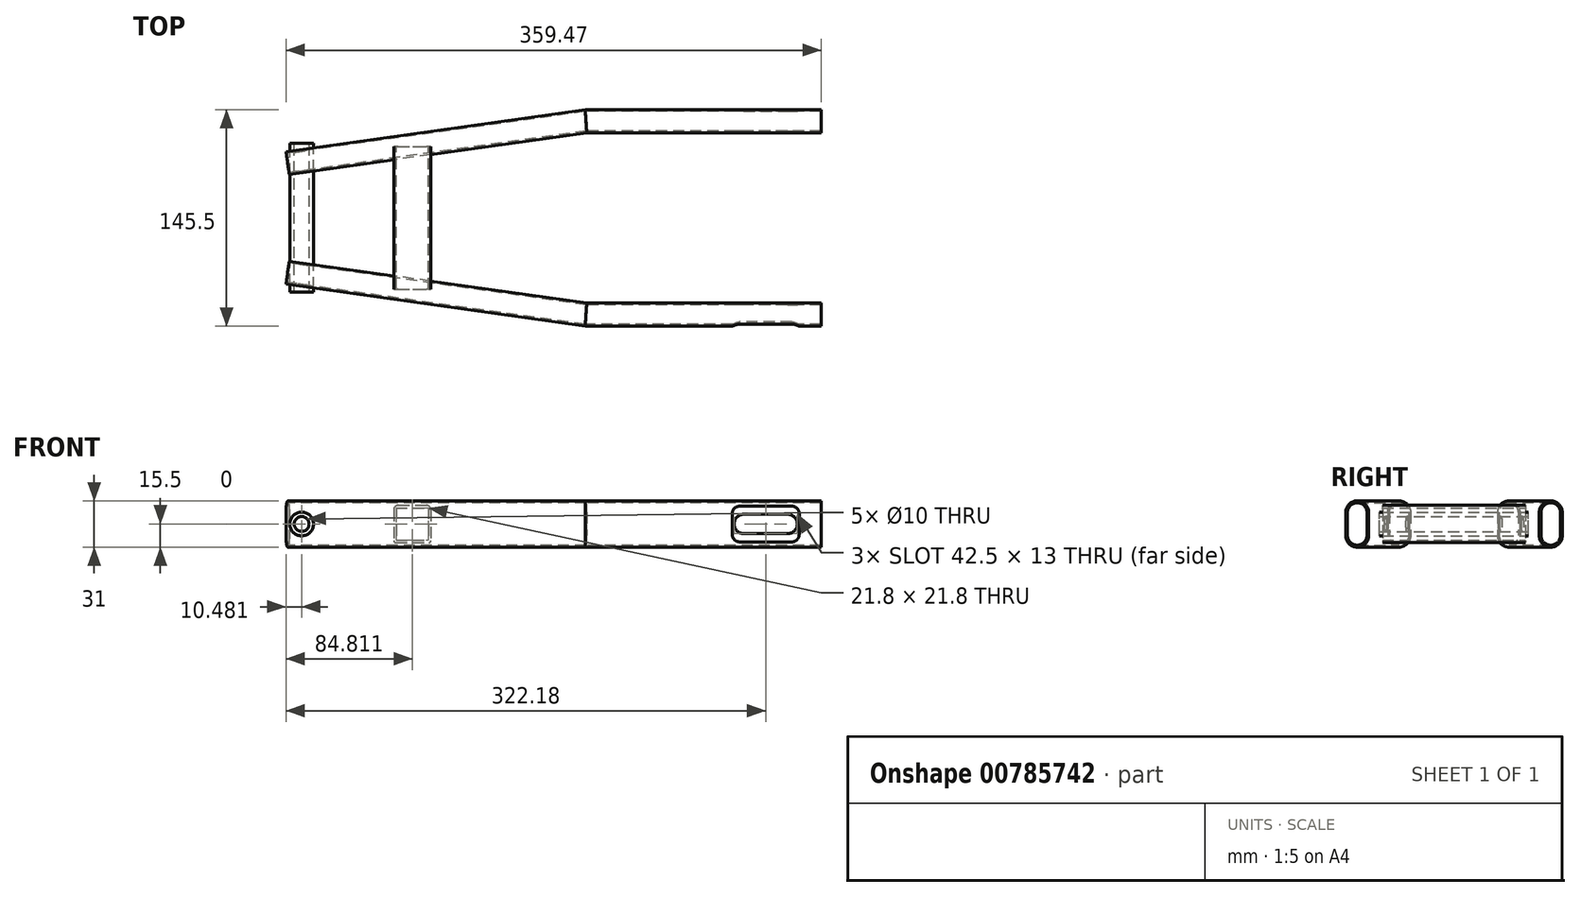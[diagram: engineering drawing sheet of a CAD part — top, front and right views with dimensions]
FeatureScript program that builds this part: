
annotation { "Feature Type Name" : "Feature", "Feature Type Description" : "" }
export const myFeature = defineFeature(function(context is Context, id is Id, definition is map)
    precondition{}
    {
        {
            var Q0;
            Q0=qCreatedBy(makeId("Top.planeOp"),FACE);
            var sketch = newSketch(context, id + "F0", { "sketchPlane" : qUnion([Q0])});
            skLineSegment(sketch, "E0", {"start": v(0, 65) * mm, "end": v(-158, 65) * mm});
            skLineSegment(sketch, "E1", {"start": v(-158, 65) * mm, "end": v(-358.4, 36.84) * mm});
            skSolve(sketch);
        }
        {
            var Q0;
            Q0=qCreatedBy(makeId("Right.planeOp"),FACE);
            var sketch = newSketch(context, id + "F1", { "sketchPlane" : qUnion([Q0])});
            skLineSegment(sketch, "E2.left", {"start": v(57.25, 7.75) * mm, "end": v(57.25, -7.75) * mm});
            skLineSegment(sketch, "E2.right", {"start": v(72.75, 7.75) * mm, "end": v(72.75, -7.75) * mm});
            skPoint(sketch, "E2.middle", {"position": v(65, 0) * mm});
            skArc(sketch, "E3", {"start": v(57.25, -7.75) * mm, "mid": v(65, -15.5) * mm, "end": v(72.75, -7.75) * mm});
            skArc(sketch, "E4", {"start": v(57.25, 7.75) * mm, "mid": v(65, 15.5) * mm, "end": v(72.75, 7.75) * mm});
            skLineSegment(sketch, "E5.0", {"start": v(71.55, 7.75) * mm, "end": v(71.55, -7.75) * mm});
            skLineSegment(sketch, "E6.0", {"start": v(58.45, 7.75) * mm, "end": v(58.45, -7.75) * mm});
            skArc(sketch, "E7.0", {"start": v(58.45, 7.75) * mm, "mid": v(65, 14.3) * mm, "end": v(71.55, 7.75) * mm});
            skArc(sketch, "E8.0", {"start": v(58.45, -7.75) * mm, "mid": v(65, -14.3) * mm, "end": v(71.55, -7.75) * mm});
            skSolve(sketch);
        }
        {
            var Q0;
            Q0=qSketchRegion(id+"F1",true);
            var Q1;
            Q1=qConstructionFilter(qBodyType(qCreatedBy(id+"F0",EDGE),BodyType.WIRE),ConstructionObject.NO);
            sweep(context, id + "F2", {"profiles" : qUnion([Q0]), "path" : qUnion([Q1])});
        }
        {
            var Q0;
            Q0=makeQuery(id+"F2.opSweep","SWEPT_BODY",BODY,{"disambiguationData":[OSD([sQuery(id+"F0.wireOp",EDGE,"E1"),sQuery(id+"F1.wireOp",EDGE,"E2.left"),sQuery(id+"F1.wireOp",EDGE,"E2.right"),sQuery(id+"F1.wireOp",EDGE,"E3"),sQuery(id+"F1.wireOp",EDGE,"E4"),sQuery(id+"F1.wireOp",EDGE,"E5.0"),sQuery(id+"F1.wireOp",EDGE,"E6.0"),sQuery(id+"F1.wireOp",EDGE,"E7.0"),sQuery(id+"F1.wireOp",EDGE,"E8.0")])]});
            var Q1;
            Q1=qCreatedBy(makeId("Front.planeOp"),FACE);
            mirror(context, id + "F3", {"entities" : qUnion([Q0]), "mirrorPlane" : qUnion([Q1])});
        }
        {
            var Q0;
            Q0=qCreatedBy(makeId("Front.planeOp"),FACE);
            var sketch = newSketch(context, id + "F4", { "sketchPlane" : qUnion([Q0])});
            skLineSegment(sketch, "E9.bottom", {"start": v(-52.04, 6.5) * mm, "end": v(-22.54, 6.5) * mm});
            skLineSegment(sketch, "E9.top", {"start": v(-52.04, -6.5) * mm, "end": v(-22.54, -6.5) * mm});
            skLineSegment(sketch, "E9.left", {"start": v(-52.04, 6.5) * mm, "end": v(-52.04, -6.5) * mm});
            skLineSegment(sketch, "E9.right", {"start": v(-22.54, 6.5) * mm, "end": v(-22.54, -6.5) * mm});
            skPoint(sketch, "E9.middle", {"position": v(-37.3, 0) * mm});
            skArc(sketch, "E10", {"start": v(-22.54, 6.5) * mm, "mid": v(-16.04, 0) * mm, "end": v(-22.54, -6.5) * mm});
            skArc(sketch, "E11", {"start": v(-52.04, 6.5) * mm, "mid": v(-58.54, 0) * mm, "end": v(-52.04, -6.5) * mm});
            skSolve(sketch);
        }
        {
            var Q0;
            Q0=qSketchRegion(id+"F4",true);
            extrude(context, id + "F5", {"entities" : qUnion([Q0]), "operationType" : NewBodyOperationType.REMOVE, "depth" : 99 * mm, "offsetDistance" : 25 * mm});
        }
        {
            var Q0;
            Q0=qSketchRegion(id+"F4",true);
            extrude(context, id + "F6", {"entities" : qUnion([Q0]), "operationType" : NewBodyOperationType.REMOVE, "oppositeDirection" : true, "depth" : 86 * mm, "offsetDistance" : 25 * mm});
        }
        {
            var Q0;
            Q0=qCreatedBy(makeId("Front.planeOp"),FACE);
            var sketch = newSketch(context, id + "F7", { "sketchPlane" : qUnion([Q0])});
            skCircle(sketch, "E12", {"center": v(-348.99, 0) * mm, "radius": 8 * mm});
            skCircle(sketch, "E13", {"center": v(-348.99, 0) * mm, "radius": 5 * mm});
            skSolve(sketch);
        }
        {
            var Q0;
            Q0=qSketchRegion(id+"F7",true);
            extrude(context, id + "F8", {"entities" : qUnion([Q0]), "endBound" : BoundingType.SYMMETRIC, "depth" : 100 * mm, "offsetDistance" : 25 * mm});
        }
        {
            var Q0;
            Q0=qCreatedBy(makeId("Front.planeOp"),FACE);
            var sketch = newSketch(context, id + "F9", { "sketchPlane" : qUnion([Q0])});
            skLineSegment(sketch, "E14.bottom", {"start": v(-287.16, 12.5) * mm, "end": v(-262.16, 12.5) * mm});
            skLineSegment(sketch, "E14.top", {"start": v(-287.16, -12.5) * mm, "end": v(-262.16, -12.5) * mm});
            skLineSegment(sketch, "E14.left", {"start": v(-287.16, 12.5) * mm, "end": v(-287.16, -12.5) * mm});
            skLineSegment(sketch, "E14.right", {"start": v(-262.16, 12.5) * mm, "end": v(-262.16, -12.5) * mm});
            skPoint(sketch, "E14.middle", {"position": v(-274.66, 0) * mm});
            skLineSegment(sketch, "E15.0", {"start": v(-285.56, 12.5) * mm, "end": v(-285.56, -12.5) * mm});
            skLineSegment(sketch, "E16.0", {"start": v(-287.16, 10.9) * mm, "end": v(-262.16, 10.9) * mm});
            skLineSegment(sketch, "E17.0", {"start": v(-263.76, 12.5) * mm, "end": v(-263.76, -12.5) * mm});
            skLineSegment(sketch, "E18.0", {"start": v(-287.16, -10.9) * mm, "end": v(-262.16, -10.9) * mm});
            skSolve(sketch);
        }
        {
            var Q0;
            Q0=qSketchRegion(id+"F9",true);
            extrude(context, id + "F10", {"entities" : qUnion([Q0]), "endBound" : BoundingType.SYMMETRIC, "depth" : 96 * mm, "offsetDistance" : 25 * mm});
        }
        {
            var Q0;
            Q0=makeQuery(id+"F10.opExtrude","SWEPT_EDGE",EDGE,{"disambiguationData":[OSD([sQuery(id+"F9.wireOp",EDGE,"E14.bottom"),sQuery(id+"F9.wireOp",EDGE,"E14.right")])]});
            var Q1;
            Q1=makeQuery(id+"F10.opExtrude","SWEPT_EDGE",EDGE,{"disambiguationData":[OSD([sQuery(id+"F9.wireOp",EDGE,"E14.bottom"),sQuery(id+"F9.wireOp",EDGE,"E14.left")])]});
            fillet(context, id + "F11", {"entities" : qUnion([Q0, Q1]), "radius" : 3 * mm, "tangentPropagation" : true, "allowEdgeOverflow" : false});
        }
        {
            var Q0;
            Q0=makeQuery(id+"F10.opExtrude","SWEPT_EDGE",EDGE,{"disambiguationData":[OSD([sQuery(id+"F9.wireOp",EDGE,"E14.top"),sQuery(id+"F9.wireOp",EDGE,"E14.right")])]});
            var Q1;
            Q1=makeQuery(id+"F10.opExtrude","SWEPT_EDGE",EDGE,{"disambiguationData":[OSD([sQuery(id+"F9.wireOp",EDGE,"E14.top"),sQuery(id+"F9.wireOp",EDGE,"E14.left")])]});
            fillet(context, id + "F12", {"entities" : qUnion([Q0, Q1]), "radius" : 1.4 * mm, "tangentPropagation" : true, "allowEdgeOverflow" : false});
        }
        {
            var Q0;
            Q0=makeQuery(id+"F3.opPattern","COPY",FACE,{"derivedFrom":makeQuery(id+"F2.opSweep","SWEPT_FACE",FACE,{"disambiguationData":[OSD([sQuery(id+"F0.wireOp",EDGE,"E0"),sQuery(id+"F1.wireOp",EDGE,"E2.right")])]}),"instanceName":"1"});
            var sketch = newSketch(context, id + "F13", { "sketchPlane" : qUnion([Q0])});
            skSolve(sketch);
        }
        {
            var Q0;
            {var subQ0=sQuery(id+"F1.wireOp",EDGE,"E2.right");Q0=makeQuery(id+"F13.imprint","IMPRINT",FACE,{"disambiguationData":[TD([[makeQuery(id+"F13.imprint","IMPRINT",EDGE,{"derivedFrom":makeQuery(id+"F3.opPattern","COPY",EDGE,{"derivedFrom":makeQuery(id+"F2.opSweep","CAP_EDGE",EDGE,{"disambiguationData":[OSD([sQuery(id+"F0.wireOp",VERTEX,"E0.start"),subQ0])],"isStart":true}),"instanceName":"1"})}),-1.0]])]});}
            var sketch = newSketch(context, id + "F14", { "sketchPlane" : qUnion([Q0])});
            skPoint(sketch, "E19.middle", {"position": v(-37.26, 0) * mm});
            skArc(sketch, "E20", {"start": v(-19.76, 12) * mm, "mid": v(-16.22, 10.54) * mm, "end": v(-14.76, 7) * mm});
            skArc(sketch, "E21", {"start": v(-54.76, 12) * mm, "mid": v(-58.3, 10.54) * mm, "end": v(-59.76, 7) * mm});
            skArc(sketch, "E22", {"start": v(-54.76, -12) * mm, "mid": v(-58.3, -10.54) * mm, "end": v(-59.76, -7) * mm});
            skArc(sketch, "E23", {"start": v(-19.76, -12) * mm, "mid": v(-16.22, -10.54) * mm, "end": v(-14.76, -7) * mm});
            skLineSegment(sketch, "E24", {"start": v(-54.76, 12) * mm, "end": v(-19.76, 12) * mm});
            skLineSegment(sketch, "E25", {"start": v(-14.76, 7) * mm, "end": v(-14.76, -7) * mm});
            skLineSegment(sketch, "E26", {"start": v(-19.76, -12) * mm, "end": v(-54.76, -12) * mm});
            skLineSegment(sketch, "E27", {"start": v(-59.76, -7) * mm, "end": v(-59.76, 7) * mm});
            skSolve(sketch);
        }
        {
            var Q0;
            Q0=qSketchRegion(id+"F14",true);
            extrude(context, id + "F15", {"entities" : qUnion([Q0]), "operationType" : NewBodyOperationType.REMOVE, "oppositeDirection" : true, "depth" : 8 * mm, "offsetDistance" : 25 * mm});
        }
        {
            var Q0;
            Q0=makeQuery(id+"F8.opExtrude","CAP_FACE",FACE,{"disambiguationData":[OSD([sQuery(id+"F7.wireOp",EDGE,"E12"),sQuery(id+"F7.wireOp",EDGE,"E13")])],"isStart":false});
            var sketch = newSketch(context, id + "F16", { "sketchPlane" : qUnion([Q0])});
            skCircle(sketch, "E28", {"center": v(-348.99, 0) * mm, "radius": 5 * mm});
            skSolve(sketch);
        }
        {
            var Q0;
            Q0=qSketchRegion(id+"F16",true);
            extrude(context, id + "F17", {"entities" : qUnion([Q0]), "operationType" : NewBodyOperationType.REMOVE, "endBound" : BoundingType.THROUGH_ALL, "oppositeDirection" : true, "depth" : 25 * mm, "offsetDistance" : 25 * mm});
        }
        {
            var Q0;
            Q0 = qSketchRegion(id + "F14", true);
            extrude(context, id + "F18", {"entities" : qUnion([Q0]), "operationType" : NewBodyOperationType.REMOVE, "oppositeDirection" : true, "depth" : 10 * mm, "offsetDistance" : 25 * mm});
        }
    });
